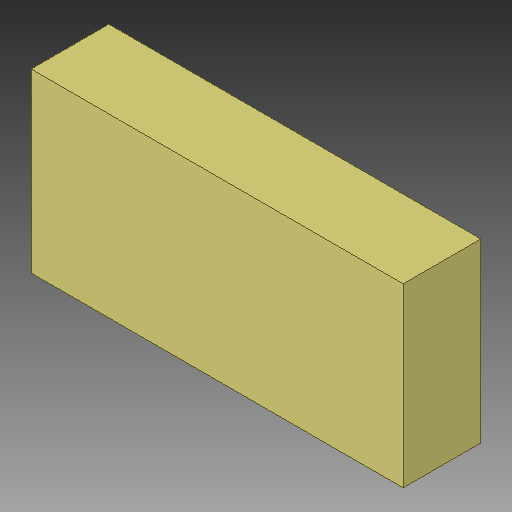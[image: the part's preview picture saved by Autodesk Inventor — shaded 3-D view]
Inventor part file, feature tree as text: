
AUTODESK INVENTOR PART (.ipt)
format: ipt  version: 2018 (Build 220112000, 112)  size: 80,384 bytes
history: native  units: in
note: dims shown in document units (in); Inventor stores cm internally (conversion verified against a paired STEP export)
features: other x1, extrude x1
ambient origin geometry x8: Origin, YZ Plane, XZ Plane, XY Plane, X Axis, Y Axis, Z Axis, Center Point
bodies: Solid1 (feature_tree)
feature tree (2):
  other  "SILK_3V3_TAG, SILK_3V3_TAG_162"
  extrude  "Extrusion1"  Depth=0.0394in TaperAngle=0.0deg
